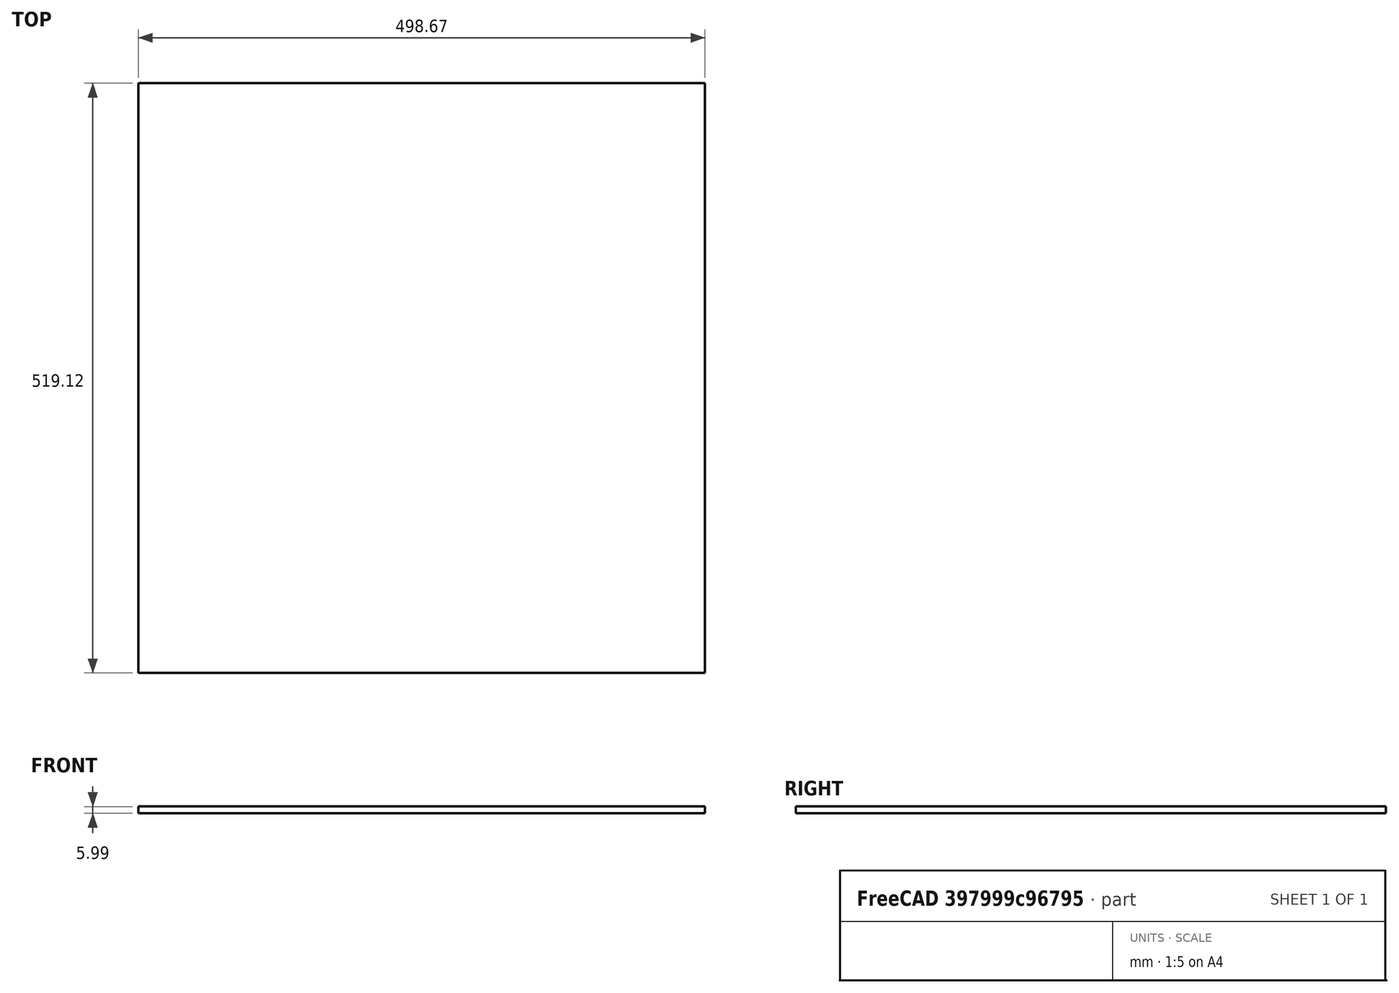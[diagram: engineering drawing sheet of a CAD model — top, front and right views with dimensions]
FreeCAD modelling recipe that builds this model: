
FCSTD DOCUMENT  (FreeCAD 0.19R24267 (Git))
Label: Up1-P7
License: All rights reserved
LicenseURL: http://en.wikipedia.org/wiki/All_rights_reserved
objects: TechDraw::DrawViewDimension×3, TechDraw::DrawProjGroupItem×2, TechDraw::DrawHatch×2, TechDraw::DrawViewAnnotation×2, Sketcher::SketchObject×1, Part::Extrusion×1, TechDraw::DrawSVGTemplate×1, TechDraw::DrawProjGroup×1, TechDraw::DrawPage×1
note: 2 computed .brp shape members not serialized (recipe doc carries the construction recipe); baked Part::Feature solids carry a one-line shape summary decoded from their .brp

FEATURE [Sketcher::SketchObject] Sketch
  FullyConstrained = false
  sketch-geometry (4):
    g0: LineSegment StartX=-88.6853 StartY=-284.242 StartZ=0 EndX=409.98 EndY=-284.242 EndZ=0
    g1: LineSegment StartX=409.98 StartY=-284.242 StartZ=0 EndX=409.98 EndY=234.883 EndZ=0
    g2: LineSegment StartX=409.98 StartY=234.883 StartZ=0 EndX=-88.6853 EndY=234.883 EndZ=0
    g3: LineSegment StartX=-88.6853 StartY=234.883 StartZ=0 EndX=-88.6853 EndY=-284.242 EndZ=0
  constraints (10):
    c: Coincident(g0,g1)
    c: Coincident(g1,g2)
    c: Coincident(g2,g3)
    c: Coincident(g3,g0)
    c: Horizontal(g0)
    c: Horizontal(g2)
    c: Vertical(g1)
    c: Vertical(g3)
    c: DistanceX(g2,g2) = 498.666
    c: DistanceY(g3,g3) = 519.125
FEATURE [Part::Extrusion] Extrude
  Base = -> Sketch
  Dir = (0,0,1)
  DirMode = 2
  FaceMakerClass = Part::FaceMakerBullseye
  LengthFwd = 5.9944
  LengthRev = 0
  Solid = true
  Symmetric = false
FEATURE [TechDraw::DrawSVGTemplate] Template
  Height = 215.9
  Orientation = 1
  Width = 279.4
FEATURE [TechDraw::DrawProjGroupItem] ProjItem  label="Front"
  CoarseView = false
  Direction = (0,0,1)
  Focus = 100
  HardHidden = false
  IsoCount = 0
  IsoHidden = false
  IsoVisible = false
  LockPosition = true
  Perspective = false
  Rotation = 0
  RotationVector = (1,0,0)
  Scale = 0.25
  ScaleType = 2
  SeamHidden = false
  SeamVisible = true
  SmoothHidden = false
  SmoothVisible = true
  Source = -> [Extrude]
  Type = 0
  X = 0
  XDirection = (1,0,0)
  Y = 0
FEATURE [TechDraw::DrawProjGroupItem] ProjItem001  label="Left"
  CoarseView = false
  Direction = (-1,0,1e-16)
  Focus = 100
  HardHidden = false
  IsoCount = 0
  IsoHidden = false
  IsoVisible = false
  LockPosition = false
  Perspective = false
  Rotation = 0
  RotationVector = (1,0,0)
  Scale = 0.25
  ScaleType = 2
  SeamHidden = false
  SeamVisible = true
  SmoothHidden = false
  SmoothVisible = true
  Source = -> [Extrude]
  Type = 1
  X = 90.225
  XDirection = (1e-16,0,1)
  Y = 0
FEATURE [TechDraw::DrawProjGroup] ProjGroup
  Anchor = -> ProjItem
  AutoDistribute = true
  LockPosition = false
  ProjectionType = 0
  Rotation = 0
  Scale = 0.25
  ScaleType = 2
  Source = -> [Extrude]
  Views = -> [ProjItem,ProjItem001]
  X = 139.7
  Y = 107.95
  spacingX = 15.0114
  spacingY = 15.0114
FEATURE [TechDraw::DrawHatch] Hatch  label="HatchF0"
  HatchPattern = <path>
  Source = -> ProjItem [Face0]
FEATURE [TechDraw::DrawHatch] Hatch001  label="Hatch001F0"
  HatchPattern = <path>
  Source = -> ProjItem001 [Face0]
FEATURE [TechDraw::DrawViewDimension] Dimension
  Arbitrary = false
  ArbitraryTolerances = false
  EqualTolerance = true
  FormatSpec = %.3f
  FormatSpecOverTolerance = %+.3f
  FormatSpecUnderTolerance = %+.3f
  Inverted = false
  LockPosition = false
  MeasureType = 1
  OverTolerance = 0
  References2D = -> [ProjItem]
  Rotation = 0
  ScaleType = 0
  TheoreticalExact = false
  Type = 1
  UnderTolerance = 0
  X = 0
  Y = -72.8597
FEATURE [TechDraw::DrawViewDimension] Dimension001
  Arbitrary = false
  ArbitraryTolerances = false
  EqualTolerance = true
  FormatSpec = %.3f
  FormatSpecOverTolerance = %+.3f
  FormatSpecUnderTolerance = %+.3f
  Inverted = false
  LockPosition = false
  MeasureType = 1
  OverTolerance = 0
  References2D = -> [ProjItem]
  Rotation = 0
  ScaleType = 0
  TheoreticalExact = false
  Type = 2
  UnderTolerance = 0
  X = 69.0493
  Y = 0.223133
FEATURE [TechDraw::DrawViewDimension] Dimension002
  Arbitrary = false
  ArbitraryTolerances = false
  EqualTolerance = true
  FormatSpec = %.3f
  FormatSpecOverTolerance = %+.3f
  FormatSpecUnderTolerance = %+.3f
  Inverted = false
  LockPosition = false
  MeasureType = 1
  OverTolerance = 0
  References2D = -> [ProjItem001]
  Rotation = 0
  ScaleType = 0
  TheoreticalExact = false
  Type = 1
  UnderTolerance = 0
  X = 13.7744
  Y = 57.9566
FEATURE [TechDraw::DrawViewAnnotation] Annotation
  Font = osifont
  LineSpace = 80
  LockPosition = false
  MaxWidth = -1
  Rotation = 0
  ScaleType = 0
  Text = Figure S3 (Upright) | Panel 7 [back left] | Quantity: 1
  TextSize = 5.0038
  TextStyle = 0
  X = 29.434
  Y = 195.58
FEATURE [TechDraw::DrawViewAnnotation] Annotation002
  Font = osifont
  LineSpace = 80
  LockPosition = false
  MaxWidth = -1
  Rotation = 0
  ScaleType = 0
  Text = Units: Inches
  TextSize = 5.0038
  TextStyle = 0
  X = 259.08
  Y = 5.08
FEATURE [TechDraw::DrawPage] Page
  KeepUpdated = true
  NextBalloonIndex = 1
  ProjectionType = 0
  Template = -> Template
  Views = -> [ProjGroup,Dimension,Dimension001,Dimension002,Annotation,Annotation002]
note: 2 file-system paths scrubbed to <path> (originals preserved in the JSON sidecar)
